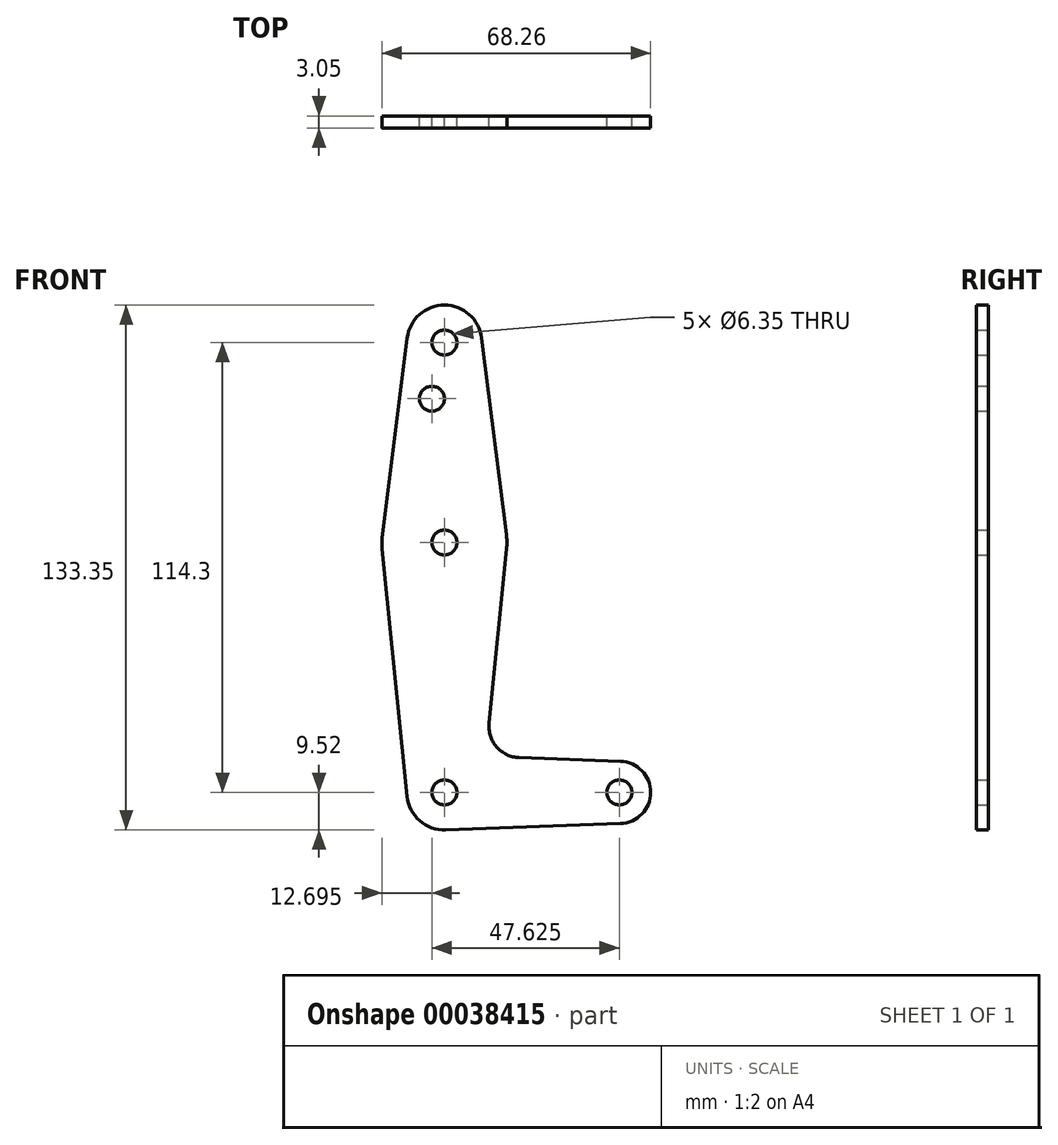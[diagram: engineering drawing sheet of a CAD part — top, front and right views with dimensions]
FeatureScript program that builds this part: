
annotation { "Feature Type Name" : "Feature", "Feature Type Description" : "" }
export const myFeature = defineFeature(function(context is Context, id is Id, definition is map)
    precondition{}
    {
        {
            var Q0;
            Q0=qCreatedBy(makeId("Front.planeOp"),FACE);
            var sketch = newSketch(context, id + "F0", { "sketchPlane" : qUnion([Q0])});
            skLineSegment(sketch, "E0", {"start": v(0, 0) * mm, "end": v(0, 114.3) * mm, "construction": true});
            skLineSegment(sketch, "E1", {"start": v(0, 0) * mm, "end": v(44.45, 0) * mm, "construction": true});
            skCircle(sketch, "E2", {"center": v(0, 114.3) * mm, "radius": 9.53 * mm});
            skCircle(sketch, "E3", {"center": v(0, 63.5) * mm, "radius": 15.88 * mm});
            skCircle(sketch, "E4", {"center": v(0, 0) * mm, "radius": 9.53 * mm});
            skCircle(sketch, "E5", {"center": v(44.45, 0) * mm, "radius": 7.94 * mm});
            skLineSegment(sketch, "E6", {"start": v(-9.45, 115.5) * mm, "end": v(-15.75, 65.48) * mm});
            skLineSegment(sketch, "E7", {"start": v(-9.48, -0.95) * mm, "end": v(-15.8, 61.91) * mm});
            skLineSegment(sketch, "E8", {"start": v(9.45, 115.5) * mm, "end": v(15.75, 65.48) * mm});
            skLineSegment(sketch, "E9", {"start": v(11.34, 17.6) * mm, "end": v(15.8, 61.91) * mm});
            skLineSegment(sketch, "E10", {"start": v(18.97, 8.85) * mm, "end": v(44.73, 7.93) * mm});
            skLineSegment(sketch, "E11", {"start": v(0.34, -9.52) * mm, "end": v(44.73, -7.93) * mm});
            skCircle(sketch, "E12", {"center": v(0, 114.3) * mm, "radius": 3.18 * mm});
            skCircle(sketch, "E13", {"center": v(-3.18, 100.03) * mm, "radius": 3.18 * mm});
            skCircle(sketch, "E14", {"center": v(0, 63.5) * mm, "radius": 3.18 * mm});
            skCircle(sketch, "E15", {"center": v(0, 0) * mm, "radius": 3.18 * mm});
            skCircle(sketch, "E16", {"center": v(44.45, 0) * mm, "radius": 3.18 * mm});
            skArc(sketch, "E17.filletArc", {"start": v(11.34, 17.6) * mm, "mid": v(13.26, 11.57) * mm, "end": v(18.97, 8.85) * mm});
            skSolve(sketch);
        }
        {
            var Q0;
            Q0 = qSketchRegion(id + "F0", true);
            extrude(context, id + "F1", {"entities" : qUnion([Q0]), "depth" : 3.05 * mm});
        }
    });
